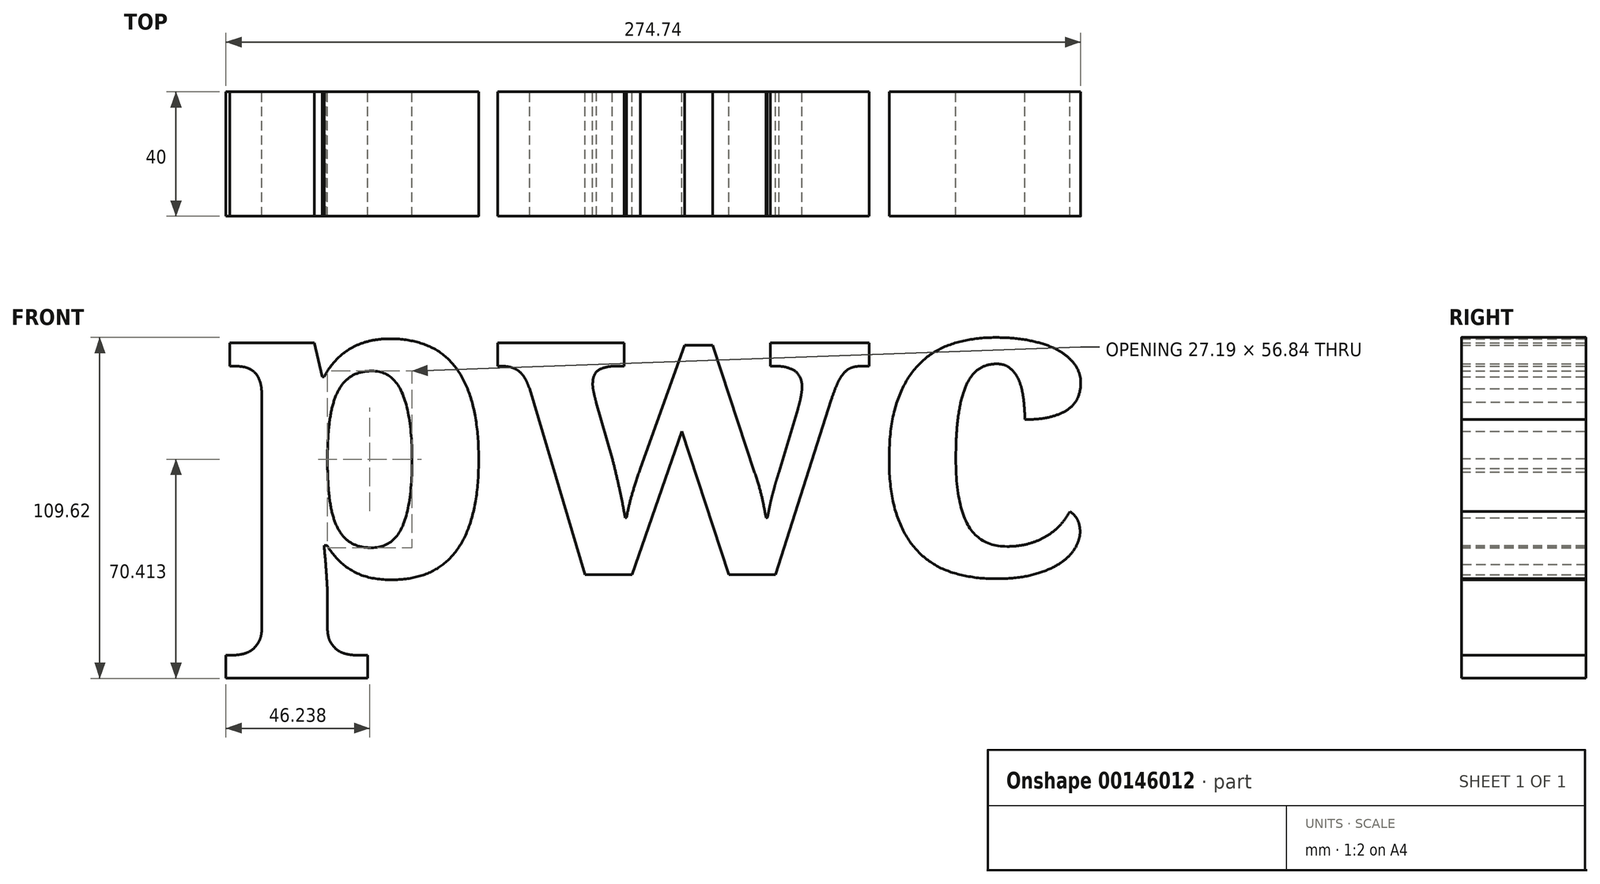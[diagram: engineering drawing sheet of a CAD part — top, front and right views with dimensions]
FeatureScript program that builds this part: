
annotation { "Feature Type Name" : "Feature", "Feature Type Description" : "" }
export const myFeature = defineFeature(function(context is Context, id is Id, definition is map)
    precondition{}
    {
        {
            var Q0;
            Q0=qCreatedBy(makeId("Front.planeOp"),FACE);
            var sketch = newSketch(context, id + "F0", { "sketchPlane" : qUnion([Q0])});
            skText(sketch, "E0", { "text": "pwc", "fontName": "NotoSerif-Bold.ttf"});
            const initialGuessF0  = {"E0": [-0.17097, -0.15538, 1, 0, 0.1]};
            skSetInitialGuess(sketch, initialGuessF0);
            skSolve(sketch);
        }
        {
            var Q0;
            Q0 = qSketchRegion(id + "F0", true);
            extrude(context, id + "F1", {"entities" : qUnion([Q0]), "depth" : 40 * mm});
        }
    });
